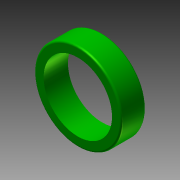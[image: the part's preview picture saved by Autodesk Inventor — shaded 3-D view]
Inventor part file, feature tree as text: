
AUTODESK INVENTOR PART (.ipt)
format: ipt  version: 2012 (Build 160160000, 160)  size: 103,424 bytes
history: native  units: in
note: dims shown in document units (in); Inventor stores cm internally (conversion verified against a paired STEP export)
features: extrude x1, fillet x1, sketch x1
ambient origin geometry x8: Origin, YZ Plane, XZ Plane, XY Plane, X Axis, Y Axis, Z Axis, Center Point
bodies: Solid1 (feature_tree)
feature tree (3):
  extrude  "Extrusion1"  Depth=2.875in
  fillet  "Fillet1"  Radius=0.8in
  sketch  "Sketch1"  dims[d0=2.25in d1=2.875in d2=0.8in d3=0.0in d4=0.0625in]
